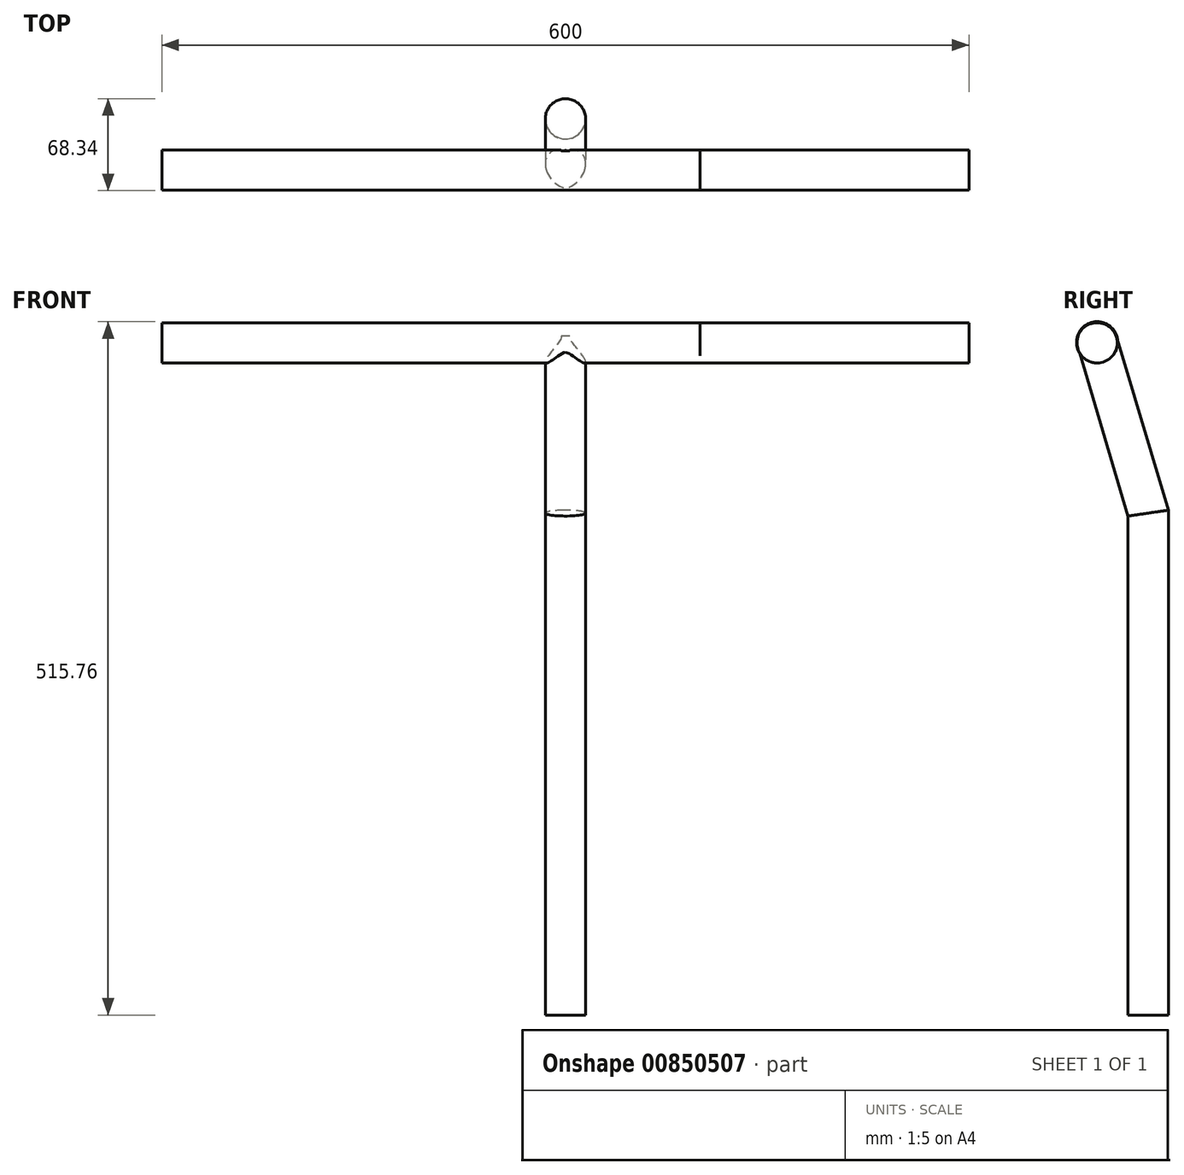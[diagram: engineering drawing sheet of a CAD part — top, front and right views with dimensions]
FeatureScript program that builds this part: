
annotation { "Feature Type Name" : "Feature", "Feature Type Description" : "" }
export const myFeature = defineFeature(function(context is Context, id is Id, definition is map)
    precondition{}
    {
        {
            var Q0;
            Q0=qCreatedBy(makeId("Top.planeOp"),FACE);
            var sketch = newSketch(context, id + "F0", { "sketchPlane" : qUnion([Q0])});
            skCircle(sketch, "E0", {"center": v(0, 0) * mm, "radius": 15 * mm});
            skSolve(sketch);
        }
        {
            var Q0;
            Q0=qCreatedBy(makeId("Right.planeOp"),FACE);
            var sketch = newSketch(context, id + "F1", { "sketchPlane" : qUnion([Q0])});
            skCircle(sketch, "E1", {"center": v(0, 500) * mm, "radius": 15 * mm});
            skSolve(sketch);
        }
        {
            var Q0;
            Q0 = qSketchRegion(id + "F1", true);
            extrude(context, id + "F2", {"entities" : qUnion([Q0]), "depth" : 300 * mm, "offsetDistance" : 25 * mm, "hasSecondDirection" : true, "secondDirectionOppositeDirection" : true, "secondDirectionDepth" : 300 * mm});
        }
        {
            var Q0;
            Q0=qCreatedBy(makeId("Right.planeOp"),FACE);
            var sketch = newSketch(context, id + "F3", { "sketchPlane" : qUnion([Q0])});
            skLineSegment(sketch, "E2", {"start": v(0, 500.85) * mm, "end": v(37.98, 373.35) * mm});
            skLineSegment(sketch, "E3", {"start": v(37.98, 373.35) * mm, "end": v(37.98, 0) * mm});
            skSolve(sketch);
        }
        {
            var Q0;
            Q0=qCreatedBy(makeId("Top.planeOp"),FACE);
            var sketch = newSketch(context, id + "F4", { "sketchPlane" : qUnion([Q0])});
            skCircle(sketch, "E4", {"center": v(0, 38.04) * mm, "radius": 15 * mm});
            skSolve(sketch);
        }
        {
            var Q0;
            Q0=makeQuery(id+"F4.imprint","IMPRINT",FACE,{"disambiguationData":[TD([[makeQuery(id+"F4.imprint","IMPRINT",EDGE,{"derivedFrom":sQuery(id+"F4.wireOp",EDGE,"E4")}),1.0]])]});
            var Q1;
            Q1=sQuery(id+"F3.wireOp",EDGE,"E2");
            var Q2;
            Q2=sQuery(id+"F3.wireOp",EDGE,"E3");
            sweep(context, id + "F5", {"operationType" : NewBodyOperationType.ADD, "profiles" : qUnion([Q0]), "path" : qUnion([Q1, Q2])});
        }
        {
            var Q0;
            Q0=qCreatedBy(makeId("Right.planeOp"),FACE);
            cPlane(context, id + "F6", {"entities" : qUnion([Q0]), "cplaneType" : CPlaneType.OFFSET, "offset" : 100 * mm, "width" : 150 * mm, "height" : 150 * mm});
        }
        {
            var Q0;
            Q0=qCreatedBy(id+"F6.planeOp",FACE);
            var sketch = newSketch(context, id + "F7", { "sketchPlane" : qUnion([Q0])});
            skCircle(sketch, "E5", {"center": v(0, 500.46) * mm, "radius": 15.3 * mm});
            skCircle(sketch, "E6.0", {"center": v(0, 500.46) * mm, "radius": 15.2 * mm});
            skSolve(sketch);
        }
        {
            var Q0;
            Q0=makeQuery(id+"F7.imprint","IMPRINT",FACE,{"disambiguationData":[TD([[makeQuery(id+"F7.imprint","IMPRINT",EDGE,{"derivedFrom":sQuery(id+"F7.wireOp",EDGE,"E5")}),1.0]])]});
            extrude(context, id + "F8", {"entities" : qUnion([Q0]), "operationType" : NewBodyOperationType.ADD, "depth" : 0.1 * mm, "offsetDistance" : 25 * mm});
        }
    });
